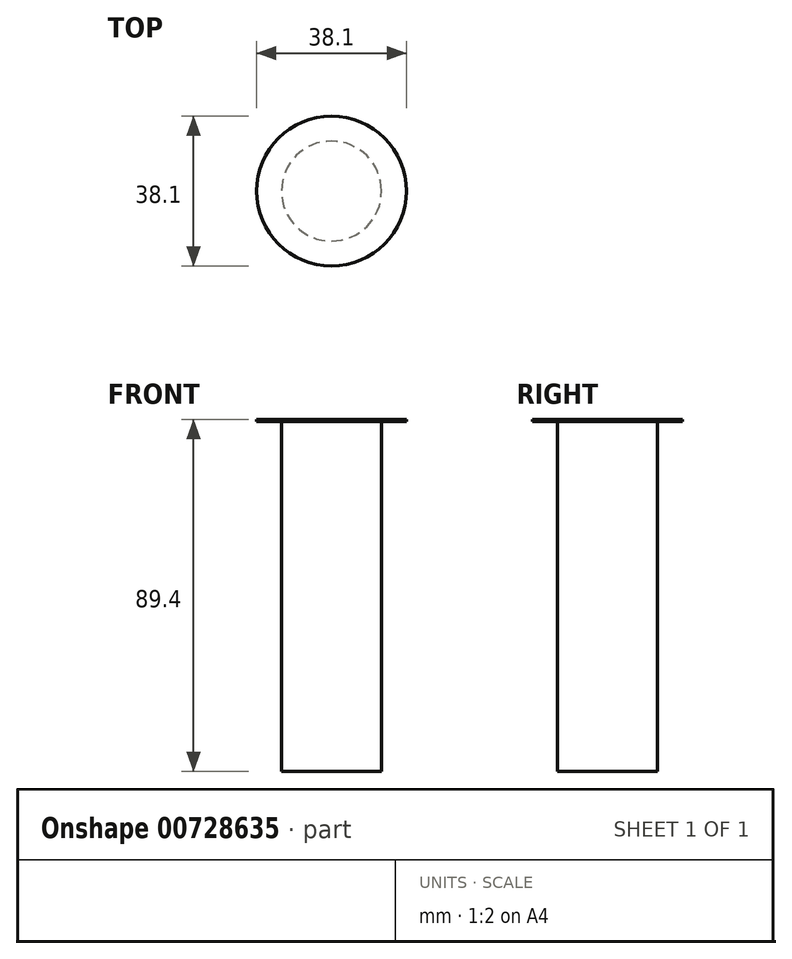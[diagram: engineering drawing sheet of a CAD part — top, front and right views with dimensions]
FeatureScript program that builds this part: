
annotation { "Feature Type Name" : "Feature", "Feature Type Description" : "" }
export const myFeature = defineFeature(function(context is Context, id is Id, definition is map)
    precondition{}
    {
        {
            assignVariable(context, id + "F0", {"name" : "pin_diam", "anyValue" : 1});
        }
        {
            assignVariable(context, id + "F1", {"name" : "head_thickness", "anyValue" : getVariable(context, 'pin_diam') / 2});
        }
        {
            var Q0;
            Q0=qCreatedBy(makeId("Top.planeOp"),FACE);
            var sketch = newSketch(context, id + "F2", { "sketchPlane" : qUnion([Q0])});
            skCircle(sketch, "E0", {"center": v(0, 0) * mm, "radius": 12.7 * mm});
            skSolve(sketch);
        }
        {
            var Q0;
            Q0 = qSketchRegion(id + "F2", true);
            extrude(context, id + "F3", {"entities" : qUnion([Q0]), "endBound" : BoundingType.SYMMETRIC, "depth" : 88.9 * mm, "offsetDistance" : 25.4 * mm});
        }
        {
            var Q0;
            Q0=makeQuery(id+"F3.opExtrude","CAP_FACE",FACE,{"disambiguationData":[OSD([sQuery(id+"F2.wireOp",EDGE,"E0")])],"isStart":false});
            var sketch = newSketch(context, id + "F4", { "sketchPlane" : qUnion([Q0])});
            skCircle(sketch, "E1", {"center": v(0, 0) * mm, "radius": 19.05 * mm});
            skSolve(sketch);
        }
        {
            var Q0;
            Q0 = qSketchRegion(id + "F4", true);
            extrude(context, id + "F5", {"entities" : qUnion([Q0]), "operationType" : NewBodyOperationType.ADD, "depth" : (getVariable(context, 'head_thickness')) * mm, "offsetDistance" : 25.4 * mm});
        }
    });
